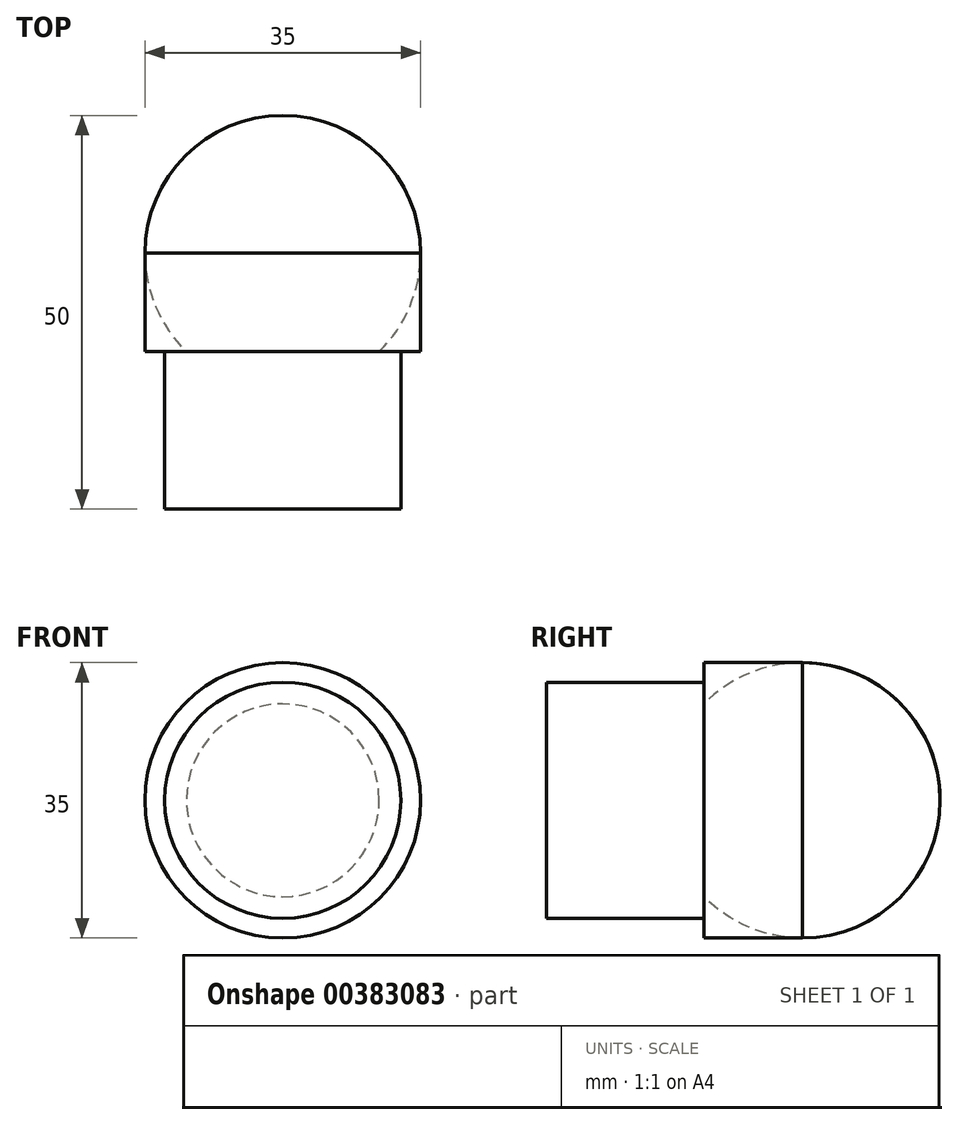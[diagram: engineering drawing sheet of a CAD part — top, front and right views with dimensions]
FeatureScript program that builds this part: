
annotation { "Feature Type Name" : "Feature", "Feature Type Description" : "" }
export const myFeature = defineFeature(function(context is Context, id is Id, definition is map)
    precondition{}
    {
        {
            var Q0;
            Q0=qCreatedBy(makeId("Right.planeOp"),FACE);
            var sketch = newSketch(context, id + "F0", { "sketchPlane" : qUnion([Q0])});
            skLineSegment(sketch, "E0", {"start": v(-25.2, 0) * mm, "end": v(24.8, 0) * mm});
            skLineSegment(sketch, "E1.bottom", {"start": v(-25.2, 0) * mm, "end": v(-5.2, 0) * mm});
            skLineSegment(sketch, "E1.top", {"start": v(-25.2, 15) * mm, "end": v(-5.2, 15) * mm});
            skLineSegment(sketch, "E1.left", {"start": v(-25.2, 0) * mm, "end": v(-25.2, 15) * mm});
            skLineSegment(sketch, "E1.right", {"start": v(-5.2, 0) * mm, "end": v(-5.2, 15) * mm});
            skLineSegment(sketch, "E2.bottom", {"start": v(-5.2, 0) * mm, "end": v(7.3, 0) * mm});
            skLineSegment(sketch, "E2.top", {"start": v(-5.2, 17.5) * mm, "end": v(7.3, 17.5) * mm});
            skLineSegment(sketch, "E2.left", {"start": v(-5.2, 0) * mm, "end": v(-5.2, 17.5) * mm});
            skLineSegment(sketch, "E2.right", {"start": v(7.3, 0) * mm, "end": v(7.3, 17.5) * mm});
            skCircle(sketch, "E3", {"center": v(7.3, 0) * mm, "radius": 17.5 * mm});
            skSolve(sketch);
        }
        {
            var Q0;
            {var subQ2=sQuery(id+"F0.wireOp",EDGE,"E1.top");Q0=makeQuery(id+"F0.imprint","IMPRINT",FACE,{"disambiguationData":[TD([[makeQuery(id+"F0.imprint","IMPRINT",EDGE,{"derivedFrom":subQ2}),-1.0]])]});}
            var Q1;
            {var subQ0=sQuery(id+"F0.wireOp",EDGE,"E2.top");Q1=makeQuery(id+"F0.imprint","IMPRINT",FACE,{"disambiguationData":[TD([[makeQuery(id+"F0.imprint","IMPRINT",EDGE,{"derivedFrom":subQ0}),-1.0]])]});}
            var Q2;
            {var subQ0=sQuery(id+"F0.wireOp",EDGE,"E2.bottom");Q2=makeQuery(id+"F0.imprint","IMPRINT",FACE,{"disambiguationData":[TD([[makeQuery(id+"F0.imprint","IMPRINT",EDGE,{"derivedFrom":subQ0}),1.0]])]});}
            var Q3;
            {var subQ0=sQuery(id+"F0.wireOp",EDGE,"E0");Q3=makeQuery(id+"F0.imprint","IMPRINT",FACE,{"disambiguationData":[TD([[makeQuery(id+"F0.imprint","IMPRINT",EDGE,{"derivedFrom":subQ0}),1.0]])]});}
            var Q4;
            {var subQ1=sQuery(id+"F0.wireOp",EDGE,"E1.bottom");var subQ3=sQuery(id+"F0.wireOp",EDGE,"E3");var subQ4=makeQuery(id+"F0.imprint","INTERSECT",VERTEX,{"derivedFrom":[subQ1,subQ3]});Q4=makeQuery(id+"F0.imprint","IMPRINT",FACE,{"disambiguationData":[TD([[makeQuery(id+"F0.imprint","IMPRINT",EDGE,{"disambiguationData":[TD([[subQ4,1.0]])],"derivedFrom":subQ3}),1.0]])]});}
            var Q5;
            Q5=sQuery(id+"F0.wireOp",EDGE,"E2.bottom");
            revolve(context, id + "F1", {"entities" : qUnion([Q0, Q1, Q2, Q3, Q4]), "axis" : qUnion([Q5]), "revolveType" : RevolveType.FULL});
        }
    });
